# Revit family: Naughtone_Stng_Construct_LowStool
name_source: partatom
category: Furniture
revit_build: Autodesk Revit 2015 (Build: 20160512_1515(x64)
units: mm (PartAtom-declared; Revit-internal decimal feet)

## types (1)
- Naughtone_Stng_Construct_LowStool
    Assembly Code = E2020200
    AssetType = Movable
    BIMObjectName = Naughtone_Seating_Construct_LowStool
    Category = Pr_40_50_12_85: Stools
    Cost = 0 $
    Description = Low Stool
    DurationUnit = year
    IfcExportAs = IfcFurnishingElementType
    IfcExportType = STOOL
    Keynote = Pr_40_50_12_85
    ManufacturerName = Naughtone
    ManufacturerURL = www.naughtone.com/
    Material = Mild Steel
    Model = CON-LO
    ModelNumber = CON-LO
    ModelReference = Low Stool
    NBSDescription = Seating
    NBSReference = 45-35-72/352
    Name = Seating_Construct_LowStool_Naughtone
    NominalHeight = 450 mm  [stored 1.47638 ft]
    NominalLength = 345 mm  [stored 1.13189 ft]
    NominalWidth = 345 mm  [stored 1.13189 ft]
    ProductInformation = www.naughtone.com/portfolio-view/construct
    Shape = Circular
    Size = 345mmx345mmx450mm
    URL = www.naughtone.com/
    Uniclass2015Description = Stools
    Uniclass2015Reference = Pr_40_50_12_85
    Uniclass2015Version = Products v1.3
    Version = 1
    WarrantyDescription = Request warranty information from naughtone
    WarrantyDurationLabor = 5
    WarrantyDurationParts = 5
    WarrantyDurationUnit = year

note: [stored X ft] marks values corroborated as IEEE doubles in the binary element streams (Revit-internal decimal feet)

## geometry (parser evidence)
native form markers: Sweep x2
no freeform markers — native parametric forms only
